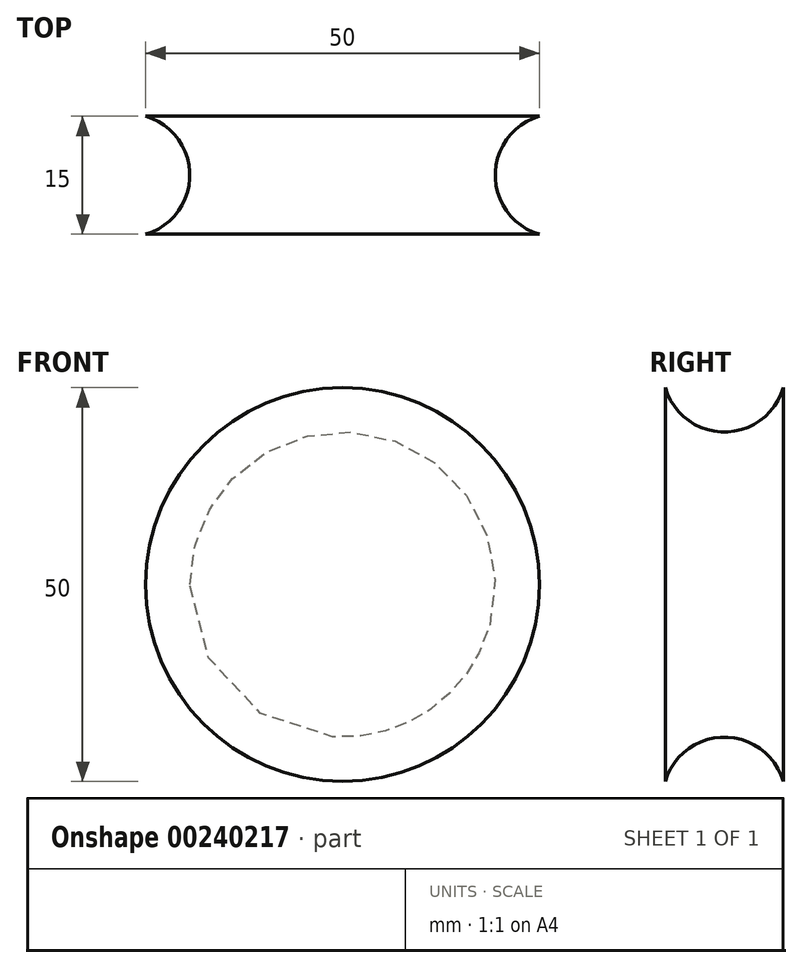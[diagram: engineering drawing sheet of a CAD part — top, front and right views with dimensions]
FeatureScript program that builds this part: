
annotation { "Feature Type Name" : "Feature", "Feature Type Description" : "" }
export const myFeature = defineFeature(function(context is Context, id is Id, definition is map)
    precondition{}
    {
        {
            var Q0;
            Q0=qCreatedBy(makeId("Top.planeOp"),FACE);
            var sketch = newSketch(context, id + "F0", { "sketchPlane" : qUnion([Q0])});
            skLineSegment(sketch, "E0", {"start": v(0.06, 7.26) * mm, "end": v(0.06, -7.74) * mm});
            skLineSegment(sketch, "E1", {"start": v(0.06, -7.74) * mm, "end": v(25.06, -7.74) * mm});
            skLineSegment(sketch, "E2", {"start": v(0.06, 7.26) * mm, "end": v(25.06, 7.26) * mm});
            skArc(sketch, "E3", {"start": v(25.06, 7.26) * mm, "mid": v(19.45, -0.24) * mm, "end": v(25.06, -7.74) * mm});
            skSolve(sketch);
        }
        {
            var Q0;
            Q0=makeQuery(id+"F0.imprint","IMPRINT",FACE,{"disambiguationData":[TD([[makeQuery(id+"F0.imprint","IMPRINT",EDGE,{"derivedFrom":sQuery(id+"F0.wireOp",EDGE,"E0")}),1.0]])]});
            var Q1;
            Q1=sQuery(id+"F0.wireOp",EDGE,"E0");
            revolve(context, id + "F1", {"entities" : qUnion([Q0]), "axis" : qUnion([Q1]), "revolveType" : RevolveType.FULL});
        }
    });
